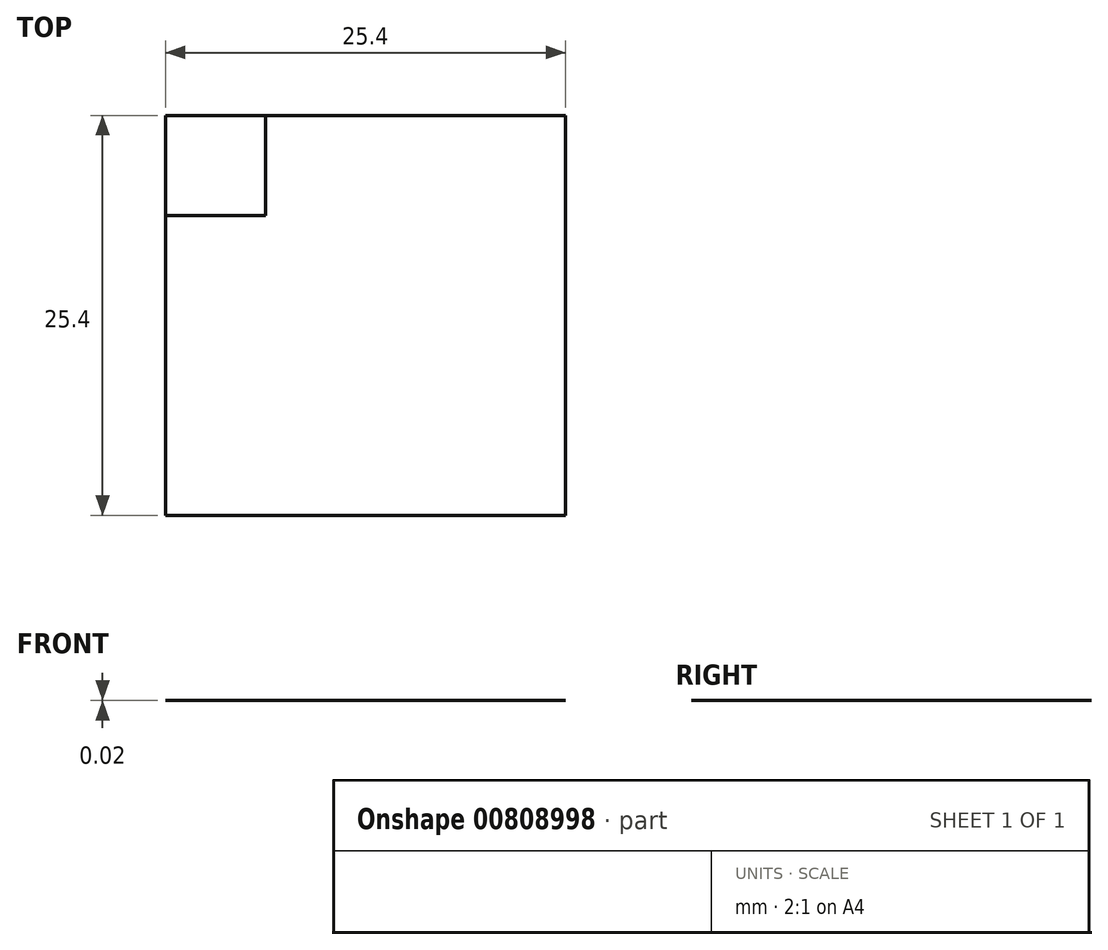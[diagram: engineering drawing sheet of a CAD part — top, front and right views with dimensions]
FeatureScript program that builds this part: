
annotation { "Feature Type Name" : "Feature", "Feature Type Description" : "" }
export const myFeature = defineFeature(function(context is Context, id is Id, definition is map)
    precondition{}
    {
        {
            var Q0;
            Q0=qCreatedBy(makeId("Top.planeOp"),FACE);
            var sketch = newSketch(context, id + "F0", { "sketchPlane" : qUnion([Q0])});
            skLineSegment(sketch, "E0.bottom", {"start": v(12.7, -12.7) * mm, "end": v(-12.7, -12.7) * mm});
            skLineSegment(sketch, "E0.top", {"start": v(12.7, 12.7) * mm, "end": v(-12.7, 12.7) * mm});
            skLineSegment(sketch, "E0.left", {"start": v(12.7, -12.7) * mm, "end": v(12.7, 12.7) * mm});
            skLineSegment(sketch, "E0.right", {"start": v(-12.7, -12.7) * mm, "end": v(-12.7, 12.7) * mm});
            skPoint(sketch, "E0.middle", {"position": v(0, 0) * mm});
            skLineSegment(sketch, "E1.bottom", {"start": v(-12.7, 12.7) * mm, "end": v(-6.35, 12.7) * mm});
            skLineSegment(sketch, "E1.top", {"start": v(-12.7, 6.35) * mm, "end": v(-6.35, 6.35) * mm});
            skLineSegment(sketch, "E1.left", {"start": v(-12.7, 12.7) * mm, "end": v(-12.7, 6.35) * mm});
            skLineSegment(sketch, "E1.right", {"start": v(-6.35, 12.7) * mm, "end": v(-6.35, 6.35) * mm});
            skSolve(sketch);
        }
        {
            var Q0;
            {var subQ1=sQuery(id+"F0.wireOp",EDGE,"E0.bottom");Q0=makeQuery(id+"F0.imprint","IMPRINT",FACE,{"disambiguationData":[TD([[makeQuery(id+"F0.imprint","IMPRINT",EDGE,{"derivedFrom":subQ1}),-1.0]])]});}
            extrude(context, id + "F1", {"entities" : qUnion([Q0]), "depth" : 1 / 406.4 * mm, "offsetDistance" : 25.4 * mm});
        }
        {
            var Q0;
            {var subQ4=sQuery(id+"F0.wireOp",EDGE,"E1.top");Q0=makeQuery(id+"F0.imprint","IMPRINT",FACE,{"disambiguationData":[TD([[makeQuery(id+"F0.imprint","IMPRINT",EDGE,{"derivedFrom":subQ4}),1.0]])]});}
            extrude(context, id + "F2", {"entities" : qUnion([Q0]), "operationType" : NewBodyOperationType.ADD, "depth" : 1 / 50.8 * mm, "offsetDistance" : 25.4 * mm});
        }
    });
